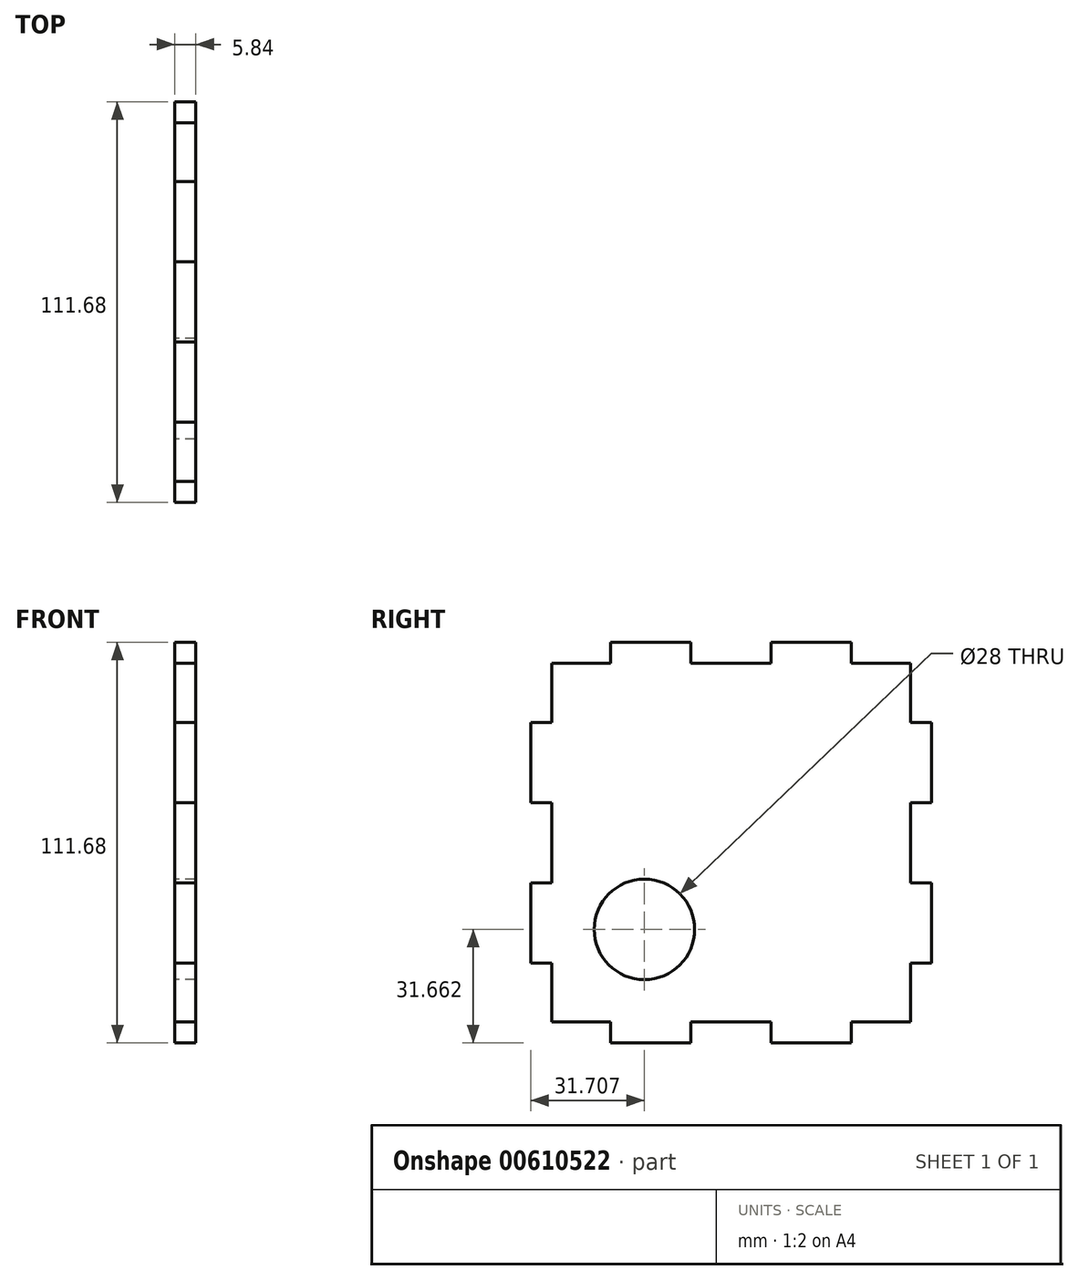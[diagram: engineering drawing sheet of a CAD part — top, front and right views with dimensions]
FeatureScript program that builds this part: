
annotation { "Feature Type Name" : "Feature", "Feature Type Description" : "" }
export const myFeature = defineFeature(function(context is Context, id is Id, definition is map)
    precondition{}
    {
        {
            var Q0;
            Q0=qCreatedBy(makeId("Right.planeOp"),FACE);
            var sketch = newSketch(context, id + "F0", { "sketchPlane" : qUnion([Q0])});
            skLineSegment(sketch, "E0.bottom", {"start": v(-50, 50) * mm, "end": v(50, 50) * mm});
            skLineSegment(sketch, "E0.top", {"start": v(-50, -50) * mm, "end": v(50, -50) * mm});
            skLineSegment(sketch, "E0.left", {"start": v(-50, 50) * mm, "end": v(-50, -50) * mm});
            skLineSegment(sketch, "E0.right", {"start": v(50, 50) * mm, "end": v(50, -50) * mm});
            skPoint(sketch, "E1.middle", {"position": v(0, 0) * mm});
            skLineSegment(sketch, "E2", {"start": v(-33.5, 50) * mm, "end": v(-33.5, 55.84) * mm});
            skLineSegment(sketch, "E3", {"start": v(-11.17, 50) * mm, "end": v(-11.17, 55.84) * mm});
            skPoint(sketch, "E3.endSnap0", {"position": v(0, 55.84) * mm});
            skLineSegment(sketch, "E4", {"start": v(11.17, 50) * mm, "end": v(11.17, 55.84) * mm});
            skLineSegment(sketch, "E5", {"start": v(33.5, 50) * mm, "end": v(33.5, 55.84) * mm});
            skLineSegment(sketch, "E6", {"start": v(-50, 33.5) * mm, "end": v(-55.84, 33.5) * mm});
            skLineSegment(sketch, "E7", {"start": v(-50, 11.17) * mm, "end": v(-55.84, 11.17) * mm});
            skLineSegment(sketch, "E8", {"start": v(-50, -11.17) * mm, "end": v(-55.84, -11.17) * mm});
            skLineSegment(sketch, "E9", {"start": v(-50, -33.5) * mm, "end": v(-55.84, -33.5) * mm});
            skLineSegment(sketch, "E10", {"start": v(-33.5, -50) * mm, "end": v(-33.5, -55.84) * mm});
            skLineSegment(sketch, "E11", {"start": v(-11.17, -50) * mm, "end": v(-11.17, -55.84) * mm});
            skLineSegment(sketch, "E12", {"start": v(11.17, -50) * mm, "end": v(11.17, -55.84) * mm});
            skLineSegment(sketch, "E13", {"start": v(33.5, -50) * mm, "end": v(33.5, -55.84) * mm});
            skLineSegment(sketch, "E14", {"start": v(50, -33.5) * mm, "end": v(55.84, -33.5) * mm});
            skLineSegment(sketch, "E15", {"start": v(50, -11.17) * mm, "end": v(55.84, -11.17) * mm});
            skLineSegment(sketch, "E16", {"start": v(50, 11.17) * mm, "end": v(55.84, 11.17) * mm});
            skLineSegment(sketch, "E17", {"start": v(50, 33.5) * mm, "end": v(55.84, 33.5) * mm});
            skLineSegment(sketch, "E18", {"start": v(55.84, 33.5) * mm, "end": v(55.84, 11.17) * mm});
            skLineSegment(sketch, "E19", {"start": v(55.84, -11.17) * mm, "end": v(55.84, -33.5) * mm});
            skLineSegment(sketch, "E20", {"start": v(11.17, -55.84) * mm, "end": v(33.5, -55.84) * mm});
            skLineSegment(sketch, "E21", {"start": v(-33.5, -55.84) * mm, "end": v(-11.17, -55.84) * mm});
            skLineSegment(sketch, "E22", {"start": v(-55.84, -33.5) * mm, "end": v(-55.84, -11.17) * mm});
            skLineSegment(sketch, "E23", {"start": v(-55.84, 33.5) * mm, "end": v(-55.84, 11.17) * mm});
            skLineSegment(sketch, "E24", {"start": v(-33.5, 55.84) * mm, "end": v(-11.17, 55.84) * mm});
            skLineSegment(sketch, "E25", {"start": v(11.17, 55.84) * mm, "end": v(33.5, 55.84) * mm});
            skPoint(sketch, "E1.left.start.orphan", {"position": v(-55.84, 55.84) * mm});
            skPoint(sketch, "E1.top.start.orphan", {"position": v(-55.84, -55.84) * mm});
            skPoint(sketch, "E26.trimOffspring.end.orphan", {"position": v(55.84, -55.84) * mm});
            skPoint(sketch, "E27.trimOffspring.end.orphan", {"position": v(55.84, 55.84) * mm});
            skCircle(sketch, "E28", {"center": v(-24.13, -24.18) * mm, "radius": 14 * mm});
            skSolve(sketch);
        }
        {
            var Q0;
            Q0=qSketchRegion(id+"F0",true);
            extrude(context, id + "F1", {"entities" : qUnion([Q0]), "depth" : 5.84 * mm, "offsetDistance" : 25 * mm});
        }
    });
